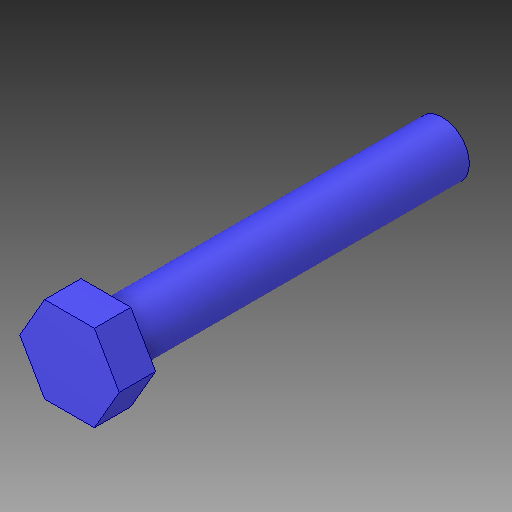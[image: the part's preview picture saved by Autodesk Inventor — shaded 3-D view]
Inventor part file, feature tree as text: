
AUTODESK INVENTOR PART (.ipt)
format: ipt  version: 2019 (Build 230136000, 136)  size: 92,672 bytes
history: mixed  units: in
note: dims shown in document units (in); Inventor stores cm internally (conversion verified against a paired STEP export)
features: extrude x1, imported_body x1
ambient origin geometry x8: Origin, YZ Plane, XZ Plane, XY Plane, X Axis, Y Axis, Z Axis, Center Point
bodies: Solid1 (imported_parasolid)
feature tree (2):
  extrude  "Extrude2"  [1 undecoded]
  imported_body  NMx_Import_Brep_tag  [imported B-rep: ~10 faces, bbox_mm=[14.780167, 12.8, 55.4]]
note: 1 required parameter value undecoded (feature->parameter linkage not recoverable at this tier; creation-order binding heuristic only, values carry confidence <= 0.55)
